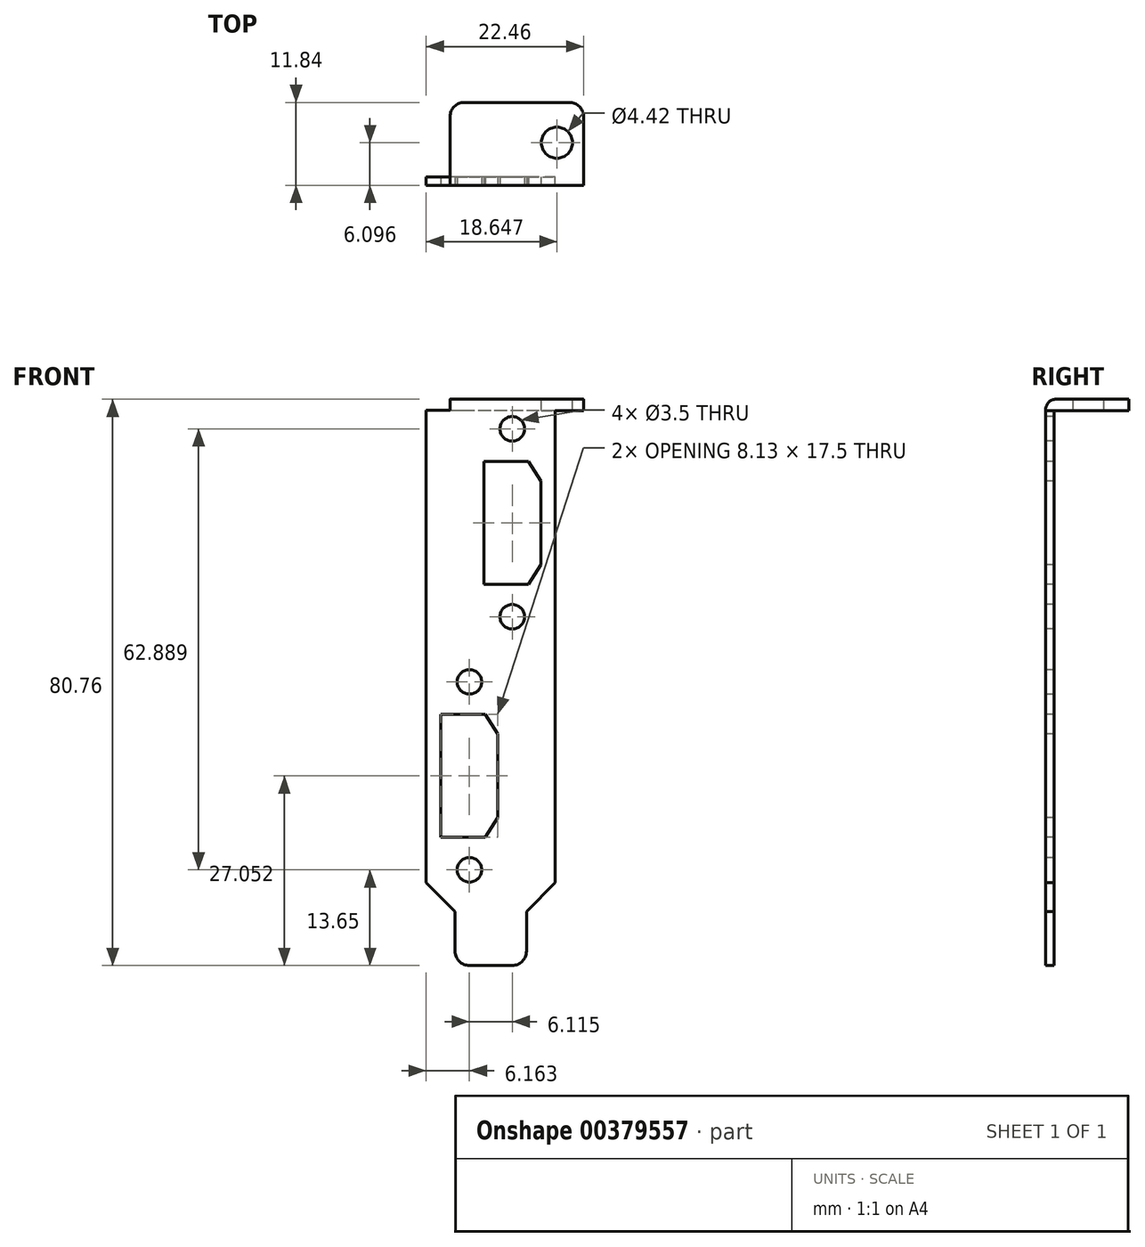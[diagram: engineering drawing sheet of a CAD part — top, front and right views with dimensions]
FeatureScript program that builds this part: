
annotation { "Feature Type Name" : "Feature", "Feature Type Description" : "" }
export const myFeature = defineFeature(function(context is Context, id is Id, definition is map)
    precondition{}
    {
        {
            var Q0;
            Q0=qCreatedBy(makeId("Front.planeOp"),FACE);
            var sketch = newSketch(context, id + "F0", { "sketchPlane" : qUnion([Q0])});
            skLineSegment(sketch, "E0.bottom", {"start": v(-22, -1.56) * mm, "end": v(-3.58, -1.56) * mm});
            skLineSegment(sketch, "E0.top", {"start": v(-15.85, -80.76) * mm, "end": v(-9.73, -80.76) * mm});
            skLineSegment(sketch, "E0.left", {"start": v(-22, -1.56) * mm, "end": v(-22, -68.92) * mm});
            skLineSegment(sketch, "E0.right", {"start": v(-3.58, -1.56) * mm, "end": v(-3.58, -68.93) * mm});
            skLineSegment(sketch, "E1", {"start": v(-17.88, -78.73) * mm, "end": v(-17.88, -73.04) * mm});
            skLineSegment(sketch, "E2", {"start": v(-17.88, -73.04) * mm, "end": v(-22, -68.92) * mm});
            skLineSegment(sketch, "E3", {"start": v(-7.7, -78.73) * mm, "end": v(-7.7, -73.04) * mm});
            skLineSegment(sketch, "E4", {"start": v(-7.7, -73.04) * mm, "end": v(-3.58, -68.93) * mm});
            skLineSegment(sketch, "E5.bottom", {"start": v(-18.6, 0) * mm, "end": v(0.46, 0) * mm});
            skLineSegment(sketch, "E5.top", {"start": v(-18.6, -1.56) * mm, "end": v(0.46, -1.56) * mm});
            skLineSegment(sketch, "E5.left", {"start": v(-18.6, 0) * mm, "end": v(-18.6, -1.56) * mm});
            skLineSegment(sketch, "E5.right", {"start": v(0.46, 0) * mm, "end": v(0.46, -1.56) * mm});
            skArc(sketch, "E6.filletArc", {"start": v(-17.88, -78.73) * mm, "mid": v(-17.29, -80.16) * mm, "end": v(-15.85, -80.76) * mm});
            skArc(sketch, "E7.filletArc", {"start": v(-9.73, -80.76) * mm, "mid": v(-8.3, -80.16) * mm, "end": v(-7.7, -78.73) * mm});
            skLineSegment(sketch, "E8.bottom", {"start": v(-15.14, -1.97) * mm, "end": v(-15.14, -1.97) * mm});
            skLineSegment(sketch, "E9", {"start": v(-15.14, -1.97) * mm, "end": v(-15.14, -1.97) * mm, "construction": true});
            skLineSegment(sketch, "E10", {"start": v(-31.72, -68.92) * mm, "end": v(6.64, -68.92) * mm, "construction": true});
            skLineSegment(sketch, "E11.bottom", {"start": v(-15.84, 1.03) * mm, "end": v(-15.85, 1.03) * mm});
            skLineSegment(sketch, "E11.top", {"start": v(-15.43, -36.27) * mm, "end": v(-15.44, -36.27) * mm});
            skLineSegment(sketch, "E12", {"start": v(-15.85, 1.03) * mm, "end": v(-15.84, 1.03) * mm, "construction": true});
            skCircle(sketch, "E13", {"center": v(-9.72, -4.22) * mm, "radius": 1.75 * mm});
            skCircle(sketch, "E14.MirrorC", {"center": v(-9.72, -31.03) * mm, "radius": 1.75 * mm});
            skLineSegment(sketch, "E15.bottom", {"start": v(-7.44, -26.37) * mm, "end": v(-13.79, -26.37) * mm});
            skLineSegment(sketch, "E15.top", {"start": v(-7.44, -8.87) * mm, "end": v(-13.79, -8.87) * mm});
            skLineSegment(sketch, "E15.left", {"start": v(-5.66, -23.58) * mm, "end": v(-5.66, -11.67) * mm});
            skLineSegment(sketch, "E15.right", {"start": v(-13.79, -26.37) * mm, "end": v(-13.79, -8.87) * mm});
            skLineSegment(sketch, "E16", {"start": v(-7.44, -8.87) * mm, "end": v(-5.66, -11.67) * mm});
            skLineSegment(sketch, "E17.MirrorCS", {"start": v(-7.44, -26.37) * mm, "end": v(-5.66, -23.58) * mm});
            skLineSegment(sketch, "E18.bottom", {"start": v(-10.48, -31.22) * mm, "end": v(-10.5, -31.22) * mm});
            skLineSegment(sketch, "E18.top", {"start": v(-9.72, -72.5) * mm, "end": v(-9.73, -72.5) * mm});
            skLineSegment(sketch, "E19", {"start": v(-10.5, -31.22) * mm, "end": v(-10.48, -31.22) * mm, "construction": true});
            skCircle(sketch, "E20", {"center": v(-15.84, -40.3) * mm, "radius": 1.75 * mm});
            skCircle(sketch, "E21.MirrorC", {"center": v(-15.84, -67.11) * mm, "radius": 1.75 * mm});
            skLineSegment(sketch, "E22.bottom", {"start": v(-13.55, -62.46) * mm, "end": v(-19.9, -62.46) * mm});
            skLineSegment(sketch, "E22.top", {"start": v(-13.55, -44.96) * mm, "end": v(-19.9, -44.96) * mm});
            skLineSegment(sketch, "E22.left", {"start": v(-11.77, -59.66) * mm, "end": v(-11.77, -47.75) * mm});
            skLineSegment(sketch, "E22.right", {"start": v(-19.9, -62.46) * mm, "end": v(-19.9, -44.96) * mm});
            skLineSegment(sketch, "E23", {"start": v(-13.55, -44.96) * mm, "end": v(-11.77, -47.75) * mm});
            skLineSegment(sketch, "E24.MirrorCS", {"start": v(-13.55, -62.46) * mm, "end": v(-11.77, -59.66) * mm});
            skLineSegment(sketch, "E25", {"start": v(-5.66, 1.22) * mm, "end": v(-5.66, -34.18) * mm, "construction": true});
            skLineSegment(sketch, "E26", {"start": v(-19.91, -6.35) * mm, "end": v(-19.91, -66.89) * mm, "construction": true});
            skSolve(sketch);
        }
        {
            var Q0;
            Q0 = qSketchRegion(id + "F0", true);
            extrude(context, id + "F1", {"entities" : qUnion([Q0]), "oppositeDirection" : true, "depth" : 1.2 * mm});
        }
        {
            var Q0;
            Q0=qCreatedBy(makeId("Top.planeOp"),FACE);
            var sketch = newSketch(context, id + "F2", { "sketchPlane" : qUnion([Q0])});
            skLineSegment(sketch, "E27.bottom", {"start": v(0.46, 0) * mm, "end": v(-18.6, 0) * mm});
            skLineSegment(sketch, "E27.top", {"start": v(-1.57, 11.84) * mm, "end": v(-16.56, 11.84) * mm});
            skLineSegment(sketch, "E27.left", {"start": v(0.46, 0) * mm, "end": v(0.46, 3.89) * mm});
            skLineSegment(sketch, "E27.right", {"start": v(-18.6, 0) * mm, "end": v(-18.6, 9.8) * mm});
            skPoint(sketch, "E28.visualSharp", {"position": v(-18.6, 11.84) * mm});
            skArc(sketch, "E28.filletArc", {"start": v(-16.56, 11.84) * mm, "mid": v(-18, 11.24) * mm, "end": v(-18.6, 9.8) * mm});
            skPoint(sketch, "E29.visualSharp", {"position": v(0.46, 11.84) * mm});
            skArc(sketch, "E29.filletArc", {"start": v(0.46, 9.8) * mm, "mid": v(-0.14, 11.24) * mm, "end": v(-1.57, 11.84) * mm});
            skLineSegment(sketch, "E30.trimOffspring", {"start": v(0.46, 8.3) * mm, "end": v(0.46, 9.8) * mm});
            skLineSegment(sketch, "E31", {"start": v(0.46, 8.3) * mm, "end": v(0.46, 3.89) * mm});
            skLineSegment(sketch, "E32", {"start": v(6.04, 6.1) * mm, "end": v(-5.07, 6.1) * mm, "construction": true});
            skLineSegment(sketch, "E33", {"start": v(-3.35, 9.05) * mm, "end": v(-3.35, 2.9) * mm, "construction": true});
            skCircle(sketch, "E34", {"center": v(-3.35, 6.1) * mm, "radius": 2.2 * mm});
            skSolve(sketch);
        }
        {
            var Q0;
            Q0 = qSketchRegion(id + "F2", true);
            extrude(context, id + "F3", {"entities" : qUnion([Q0]), "operationType" : NewBodyOperationType.ADD, "oppositeDirection" : true, "depth" : 1.6 * mm});
        }
        {
            var Q0;
            Q0=makeQuery(id+"F1.opExtrude","CAP_EDGE",EDGE,{"disambiguationData":[OSD([sQuery(id+"F0.wireOp",EDGE,"E5.bottom")])],"isStart":true});
            fillet(context, id + "F4", {"entities" : qUnion([Q0]), "radius" : 1.4 * mm, "tangentPropagation" : true, "allowEdgeOverflow" : false});
        }
    });
